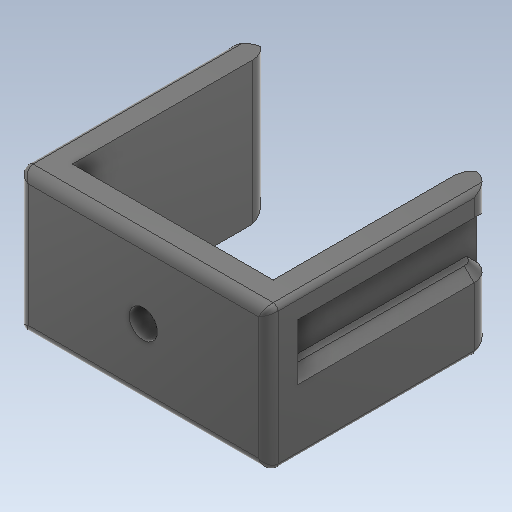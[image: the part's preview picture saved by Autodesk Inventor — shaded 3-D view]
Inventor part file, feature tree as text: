
AUTODESK INVENTOR PART (.ipt)
format: ipt  version: 2020 (Build 240168000, 168)  size: 619,520 bytes
history: native  units: mm
features: extrude x10, projected_geometry x7, sketch x5, fillet x5, chamfer x1
ambient origin geometry x8: Origin, YZ Plane, XZ Plane, XY Plane, X Axis, Y Axis, Z Axis, Center Point
bodies: Body1 (feature_tree)
feature tree (28):
  extrude  "Выдавливание7"  Depth=4.0mm
  extrude  "Выдавливание16"  Depth=25.5mm
  sketch  "Эскиз12"
  extrude  "Выдавливание17"  Depth=3.0mm
  extrude  "Выдавливание18"  Depth=3.0mm
  extrude  "Выдавливание19"  Depth=3.0mm
  fillet  "Сопряжение1"  Radius=20.2mm
  extrude  "Выдавливание20"  Depth=14.0mm TaperAngle=0.0deg
  fillet  "Сопряжение2"  Radius=26.0mm
  extrude  "Выдавливание21"  Depth=20.5mm
  extrude  "Выдавливание22"  Depth=3.0mm
  extrude  "Выдавливание23"  Depth=1.5mm
  extrude  "Выдавливание24"  Depth=0.5mm
  fillet  "Сопряжение3"  Radius=0.5mm
  fillet  "Сопряжение4"  Radius=0.5mm
  fillet  "Сопряжение5"  [1 undecoded]
  chamfer  "Фаска1"  Distance=20.0mm
  sketch  "Эскиз1"
  sketch  "Эскиз10"
  projected_geometry  "Спроецированная петля9"
  projected_geometry  "Спроецированная петля10"
  projected_geometry  "Спроецированная петля11"
  projected_geometry  "Спроецированная петля12"
  projected_geometry  "Спроецированная петля13"
  sketch  "Эскиз14"
  projected_geometry  "Спроецированная петля15"
  sketch  "Эскиз16"
  projected_geometry  "Спроецированная петля16"
note: 1 required parameter value undecoded (feature->parameter linkage not recoverable at this tier; creation-order binding heuristic only, values carry confidence <= 0.55)
